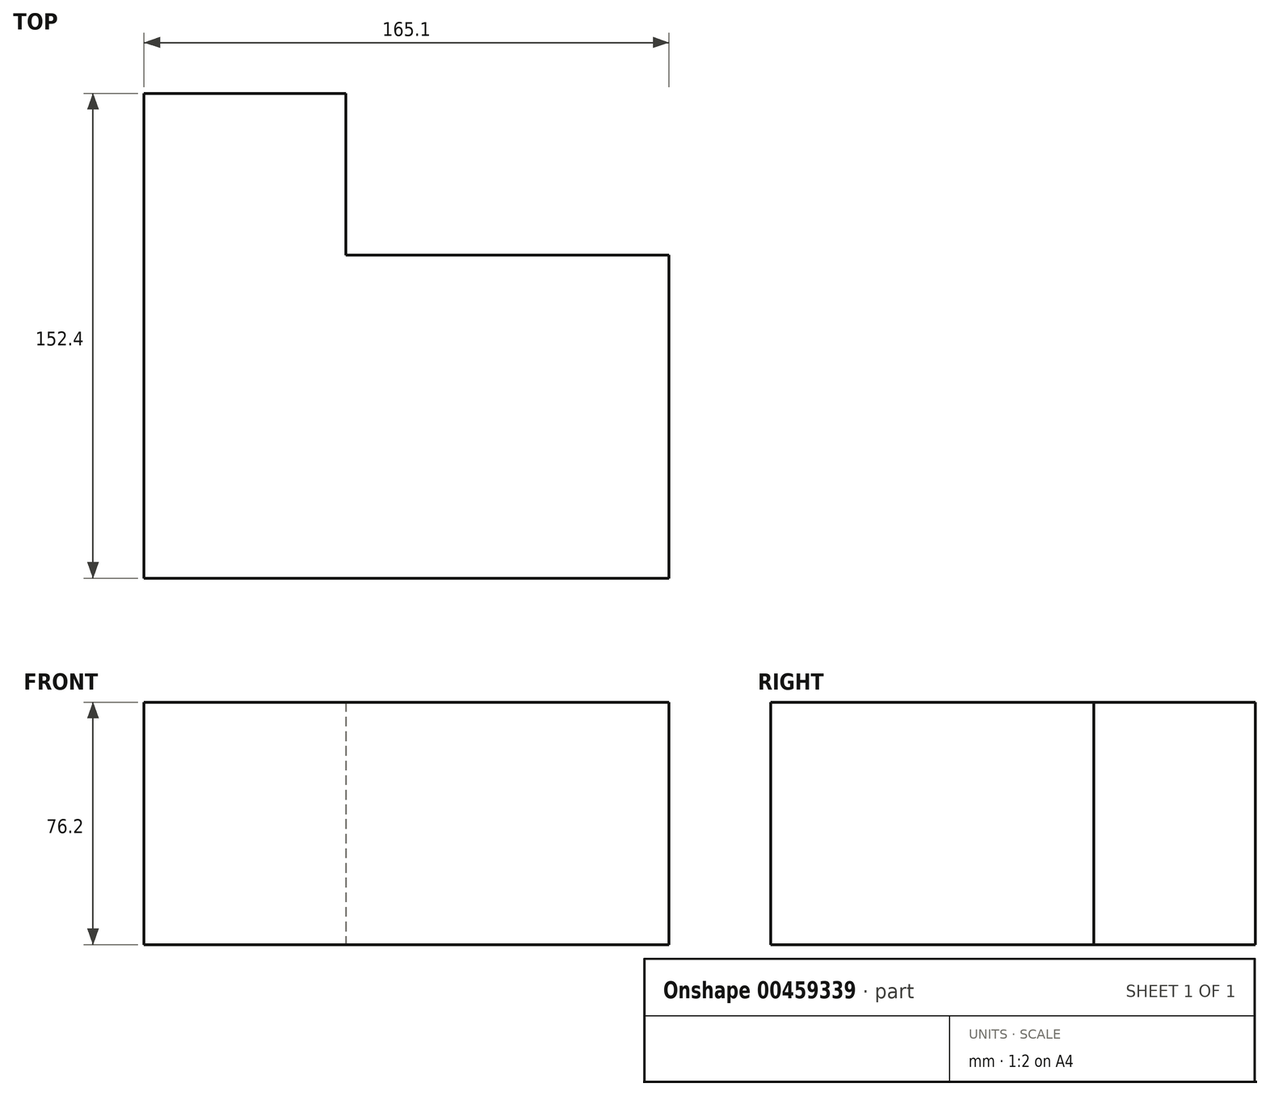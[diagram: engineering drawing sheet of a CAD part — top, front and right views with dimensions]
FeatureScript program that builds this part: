
annotation { "Feature Type Name" : "Feature", "Feature Type Description" : "" }
export const myFeature = defineFeature(function(context is Context, id is Id, definition is map)
    precondition{}
    {
        {
            var Q0;
            Q0=qCreatedBy(makeId("Front.planeOp"),FACE);
            var sketch = newSketch(context, id + "F0", { "sketchPlane" : qUnion([Q0])});
            skLineSegment(sketch, "E0.bottom", {"start": v(-114.3, 76.2) * mm, "end": v(114.3, 76.2) * mm});
            skLineSegment(sketch, "E0.top", {"start": v(-114.3, -76.2) * mm, "end": v(114.3, -76.2) * mm});
            skLineSegment(sketch, "E0.left", {"start": v(-114.3, 76.2) * mm, "end": v(-114.3, -76.2) * mm});
            skLineSegment(sketch, "E0.right", {"start": v(114.3, 76.2) * mm, "end": v(114.3, -76.2) * mm});
            skPoint(sketch, "E0.middle", {"position": v(0, 0) * mm});
            skLineSegment(sketch, "E1.bottom", {"start": v(114.3, 76.2) * mm, "end": v(-50.8, 76.2) * mm});
            skLineSegment(sketch, "E1.top", {"start": v(114.3, 0) * mm, "end": v(-50.8, 0) * mm});
            skLineSegment(sketch, "E1.left", {"start": v(114.3, 76.2) * mm, "end": v(114.3, 0) * mm});
            skLineSegment(sketch, "E1.right", {"start": v(-50.8, 76.2) * mm, "end": v(-50.8, 0) * mm});
            skSolve(sketch);
        }
        {
            var Q0;
            Q0=makeQuery(id+"F0.imprint","IMPRINT",FACE,{"disambiguationData":[TD([[makeQuery(id+"F0.imprint","IMPRINT",EDGE,{"derivedFrom":sQuery(id+"F0.wireOp",EDGE,"E0.bottom")}),-1.0]])]});
            extrude(context, id + "F1", {"entities" : qUnion([Q0]), "endBound" : BoundingType.SYMMETRIC, "depth" : 152.4 * mm});
        }
        {
            var Q0;
            Q0=makeQuery(id+"F1.opExtrude","SWEPT_FACE",FACE,{"disambiguationData":[OSD([sQuery(id+"F0.wireOp",EDGE,"E1.top")])]});
            var sketch = newSketch(context, id + "F2", { "sketchPlane" : qUnion([Q0])});
            skLineSegment(sketch, "E2.bottom", {"start": v(114.3, -76.2) * mm, "end": v(12.7, -76.2) * mm});
            skLineSegment(sketch, "E2.top", {"start": v(114.3, -25.4) * mm, "end": v(12.7, -25.4) * mm});
            skLineSegment(sketch, "E2.left", {"start": v(114.3, -76.2) * mm, "end": v(114.3, -25.4) * mm});
            skLineSegment(sketch, "E2.right", {"start": v(12.7, -76.2) * mm, "end": v(12.7, -25.4) * mm});
            skSolve(sketch);
        }
        {
            var Q0;
            Q0=makeQuery(id+"F2.imprint","IMPRINT",FACE,{"disambiguationData":[TD([[makeQuery(id+"F2.imprint","IMPRINT",EDGE,{"derivedFrom":sQuery(id+"F2.wireOp",EDGE,"E2.bottom")}),-1.0]])]});
            extrude(context, id + "F3", {"entities" : qUnion([Q0]), "operationType" : NewBodyOperationType.REMOVE, "endBound" : BoundingType.THROUGH_ALL, "oppositeDirection" : true, "depth" : 25.4 * mm});
        }
    });
